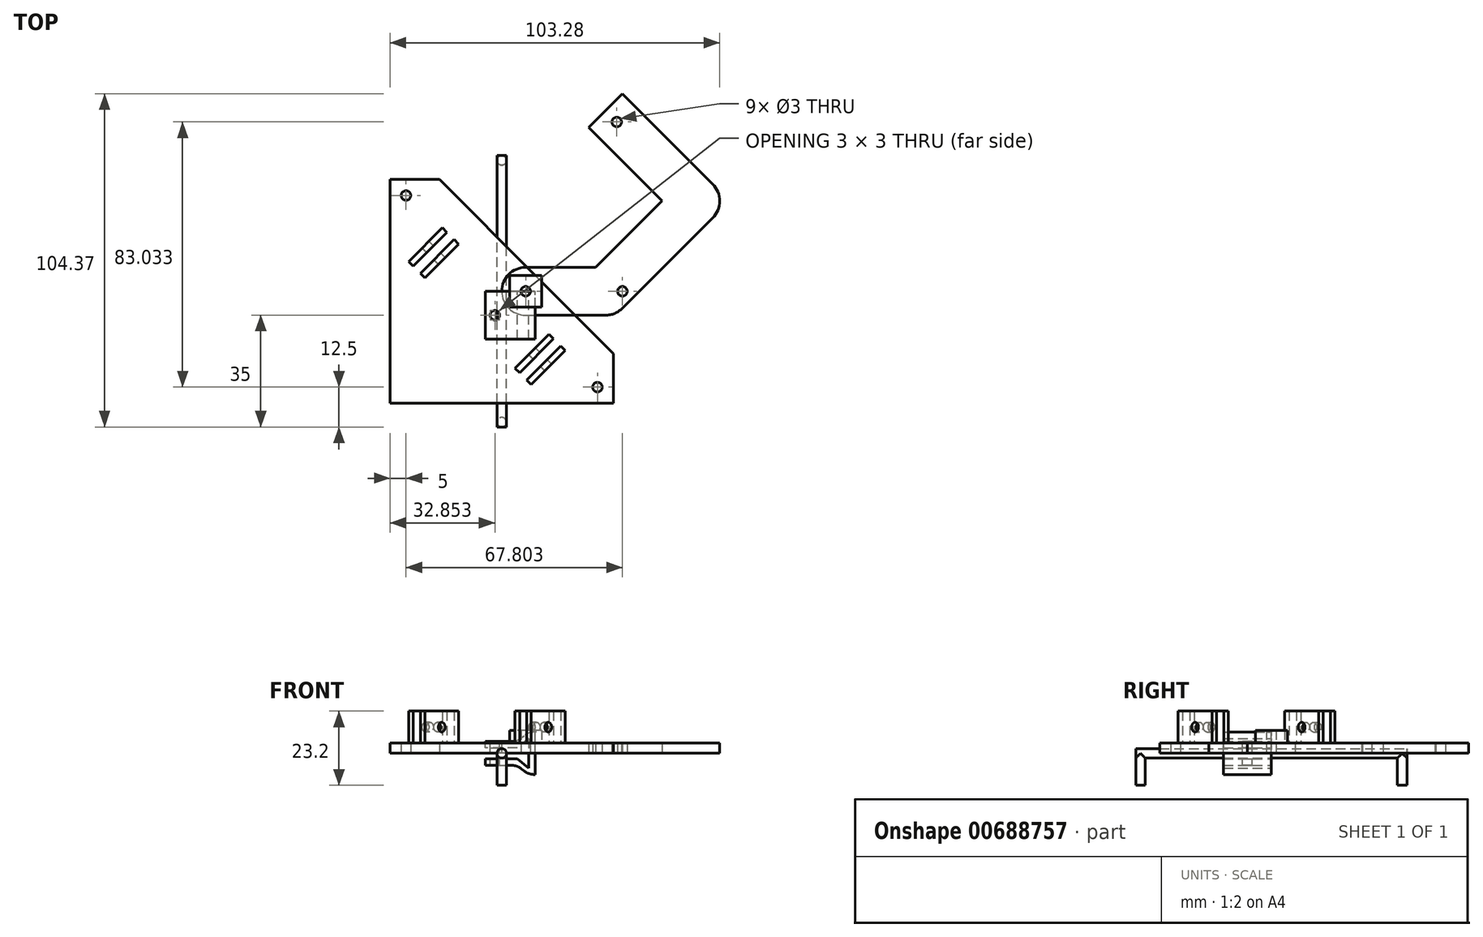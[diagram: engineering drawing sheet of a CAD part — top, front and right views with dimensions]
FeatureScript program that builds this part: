
annotation { "Feature Type Name" : "Feature", "Feature Type Description" : "" }
export const myFeature = defineFeature(function(context is Context, id is Id, definition is map)
    precondition{}
    {
        {
            var Q0;
            Q0=qCreatedBy(makeId("Top.planeOp"),FACE);
            var sketch = newSketch(context, id + "F0", { "sketchPlane" : qUnion([Q0])});
            skArc(sketch, "E0", {"start": v(7.5, 7.5) * mm, "mid": v(0, 0) * mm, "end": v(7.5, -7.5) * mm});
            skPoint(sketch, "E1", {"position": v(0, 0) * mm});
            skArc(sketch, "E2", {"start": v(32.5, -7.5) * mm, "mid": v(39.43, 2.87) * mm, "end": v(27.2, 5.3) * mm});
            skArc(sketch, "E3", {"start": v(55.48, 22.98) * mm, "mid": v(68.28, 28.28) * mm, "end": v(55.48, 33.59) * mm});
            skLineSegment(sketch, "E4", {"start": v(7.5, 7.5) * mm, "end": v(32.5, 7.5) * mm});
            skLineSegment(sketch, "E5", {"start": v(7.5, -7.5) * mm, "end": v(32.5, -7.5) * mm});
            skLineSegment(sketch, "E6", {"start": v(37.8, -5.3) * mm, "end": v(66.09, 22.98) * mm});
            skLineSegment(sketch, "E7", {"start": v(27.2, 5.3) * mm, "end": v(55.48, 33.59) * mm});
            skLineSegment(sketch, "E8", {"start": v(55.48, 22.98) * mm, "end": v(27.2, 51.27) * mm});
            skLineSegment(sketch, "E9", {"start": v(27.2, 51.27) * mm, "end": v(37.8, 61.87) * mm});
            skLineSegment(sketch, "E10", {"start": v(37.8, 61.87) * mm, "end": v(66.09, 33.59) * mm});
            skLineSegment(sketch, "E11", {"start": v(37.8, 61.87) * mm, "end": v(37.8, -5.3) * mm, "construction": true});
            skCircle(sketch, "E12", {"center": v(7.5, 0) * mm, "radius": 1.5 * mm});
            skCircle(sketch, "E13", {"center": v(37.8, 0) * mm, "radius": 1.5 * mm});
            skCircle(sketch, "E14", {"center": v(36.04, 53.03) * mm, "radius": 1.5 * mm});
            skSolve(sketch);
        }
        {
            var Q0;
            Q0=qSketchRegion(id+"F0",true);
            extrude(context, id + "F1", {"entities" : qUnion([Q0]), "depth" : 3.2 * mm, "offsetDistance" : 25 * mm});
        }
        {
            var Q0;
            Q0=qCreatedBy(makeId("Top.planeOp"),FACE);
            var sketch = newSketch(context, id + "F2", { "sketchPlane" : qUnion([Q0])});
            skLineSegment(sketch, "E15.bottom", {"start": v(35, -35) * mm, "end": v(-35, -35) * mm});
            skLineSegment(sketch, "E15.top", {"start": v(-19.55, 35) * mm, "end": v(-35, 35) * mm});
            skLineSegment(sketch, "E15.left", {"start": v(35, -35) * mm, "end": v(35, -19.55) * mm});
            skLineSegment(sketch, "E15.right", {"start": v(-35, -35) * mm, "end": v(-35, 35) * mm});
            skPoint(sketch, "E15.middle", {"position": v(0, 0) * mm});
            skCircle(sketch, "E16", {"center": v(-30, 30) * mm, "radius": 1.5 * mm});
            skCircle(sketch, "E17", {"center": v(30, -30) * mm, "radius": 1.5 * mm});
            skLineSegment(sketch, "E18", {"start": v(-35, 35) * mm, "end": v(35, -35) * mm, "construction": true});
            skLineSegment(sketch, "E19", {"start": v(-19.55, 35) * mm, "end": v(35, -19.55) * mm});
            skSolve(sketch);
        }
        {
            var Q0;
            Q0=makeQuery(id+"F2.imprint","IMPRINT",FACE,{"disambiguationData":[TD([[makeQuery(id+"F2.imprint","IMPRINT",EDGE,{"derivedFrom":sQuery(id+"F2.wireOp",EDGE,"E15.bottom")}),-1.0]])]});
            extrude(context, id + "F3", {"entities" : qUnion([Q0]), "depth" : 3.2 * mm, "offsetDistance" : 25 * mm});
        }
        {
            var Q0;
            Q0=qCreatedBy(makeId("Front.planeOp"),FACE);
            var sketch = newSketch(context, id + "F4", { "sketchPlane" : qUnion([Q0])});
            skLineSegment(sketch, "E20", {"start": v(8.43, -4.62) * mm, "end": v(4.85, -1.75) * mm});
            skLineSegment(sketch, "E21", {"start": v(4.85, -1.75) * mm, "end": v(-5.15, -1.75) * mm});
            skLineSegment(sketch, "E22", {"start": v(-5.15, -1.75) * mm, "end": v(-5.15, -3.75) * mm});
            skLineSegment(sketch, "E23", {"start": v(-5.15, -3.75) * mm, "end": v(4.85, -3.75) * mm});
            skLineSegment(sketch, "E24", {"start": v(4.85, -3.75) * mm, "end": v(8.43, -6.62) * mm});
            skLineSegment(sketch, "E25", {"start": v(8.43, -6.62) * mm, "end": v(10.43, -6.62) * mm});
            skPoint(sketch, "E26", {"position": v(8.43, 0) * mm});
            skPoint(sketch, "E27", {"position": v(10.43, 0) * mm});
            skLineSegment(sketch, "E28", {"start": v(10.43, 0) * mm, "end": v(-7.22, 0) * mm, "construction": true});
            skLineSegment(sketch, "E29", {"start": v(8.43, -4.62) * mm, "end": v(8.43, 0) * mm});
            skLineSegment(sketch, "E30", {"start": v(10.43, -6.62) * mm, "end": v(10.43, 0) * mm});
            skLineSegment(sketch, "E31.MirrorCS", {"start": v(-5.15, 1.75) * mm, "end": v(-5.15, 3.75) * mm});
            skLineSegment(sketch, "E32.MirrorCS", {"start": v(8.43, 6.62) * mm, "end": v(10.43, 6.62) * mm});
            skLineSegment(sketch, "E33.MirrorCS", {"start": v(4.85, 1.75) * mm, "end": v(-5.15, 1.75) * mm});
            skLineSegment(sketch, "E34.MirrorCS", {"start": v(8.43, 4.62) * mm, "end": v(4.85, 1.75) * mm});
            skLineSegment(sketch, "E35.MirrorCS", {"start": v(4.85, 3.75) * mm, "end": v(8.43, 6.62) * mm});
            skLineSegment(sketch, "E36.MirrorCS", {"start": v(-5.15, 3.75) * mm, "end": v(4.85, 3.75) * mm});
            skLineSegment(sketch, "E37.MirrorCS", {"start": v(8.43, 4.62) * mm, "end": v(8.43, 0) * mm});
            skLineSegment(sketch, "E38.MirrorCS", {"start": v(10.43, 6.62) * mm, "end": v(10.43, 0) * mm});
            skSolve(sketch);
        }
        {
            var Q0;
            Q0=qSketchRegion(id+"F4",true);
            extrude(context, id + "F5", {"entities" : qUnion([Q0]), "depth" : 15 * mm, "offsetDistance" : 25 * mm});
        }
        {
            var Q0;
            Q0=makeQuery(id+"F5.opExtrude","SWEPT_FACE",FACE,{"disambiguationData":[OSD([sQuery(id+"F4.wireOp",EDGE,"E36.MirrorCS")])]});
            var sketch = newSketch(context, id + "F6", { "sketchPlane" : qUnion([Q0])});
            skCircle(sketch, "E39", {"center": v(-2.15, -7.5) * mm, "radius": 1.5 * mm});
            skSolve(sketch);
        }
        {
            var Q0;
            Q0=makeQuery(id+"F6.imprint","IMPRINT",FACE,{"disambiguationData":[TD([[makeQuery(id+"F6.imprint","IMPRINT",EDGE,{"derivedFrom":sQuery(id+"F6.wireOp",EDGE,"E39")}),1.0]])]});
            extrude(context, id + "F7", {"entities" : qUnion([Q0]), "operationType" : NewBodyOperationType.REMOVE, "oppositeDirection" : true, "depth" : 25 * mm, "offsetDistance" : 25 * mm});
        }
        {
            var Q0;
            Q0=makeQuery(id+"F5.opExtrude","SWEPT_EDGE",EDGE,{"disambiguationData":[OSD([sQuery(id+"F4.wireOp",EDGE,"E35.MirrorCS"),sQuery(id+"F4.wireOp",EDGE,"E36.MirrorCS")])]});
            fillet(context, id + "F8", {"entities" : qUnion([Q0]), "radius" : 5 * mm, "tangentPropagation" : true, "allowEdgeOverflow" : false});
        }
        {
            var Q0;
            Q0=makeQuery(id+"F5.opExtrude","SWEPT_EDGE",EDGE,{"disambiguationData":[OSD([sQuery(id+"F4.wireOp",EDGE,"E23"),sQuery(id+"F4.wireOp",EDGE,"E24")])]});
            var Q1;
            Q1=makeQuery(id+"F5.opExtrude","SWEPT_EDGE",EDGE,{"disambiguationData":[OSD([sQuery(id+"F4.wireOp",EDGE,"E24"),sQuery(id+"F4.wireOp",EDGE,"E25")])]});
            var Q2;
            Q2=makeQuery(id+"F5.opExtrude","SWEPT_EDGE",EDGE,{"disambiguationData":[OSD([sQuery(id+"F4.wireOp",EDGE,"E32.MirrorCS"),sQuery(id+"F4.wireOp",EDGE,"E35.MirrorCS")])]});
            fillet(context, id + "F9", {"entities" : qUnion([Q0, Q1, Q2]), "radius" : 5 * mm, "tangentPropagation" : true, "allowEdgeOverflow" : false});
        }
        {
            var Q0;
            Q0=makeQuery(id+"F1.opExtrude","CAP_FACE",FACE,{"disambiguationData":[OSD([sQuery(id+"F0.wireOp",EDGE,"E0"),sQuery(id+"F0.wireOp",EDGE,"E2"),sQuery(id+"F0.wireOp",EDGE,"E3"),sQuery(id+"F0.wireOp",EDGE,"E4"),sQuery(id+"F0.wireOp",EDGE,"E5"),sQuery(id+"F0.wireOp",EDGE,"E6"),sQuery(id+"F0.wireOp",EDGE,"E7"),sQuery(id+"F0.wireOp",EDGE,"E8"),sQuery(id+"F0.wireOp",EDGE,"E9"),sQuery(id+"F0.wireOp",EDGE,"E10"),sQuery(id+"F0.wireOp",EDGE,"E12"),sQuery(id+"F0.wireOp",EDGE,"E13"),sQuery(id+"F0.wireOp",EDGE,"E14")])],"isStart":false});
            var sketch = newSketch(context, id + "F10", { "sketchPlane" : qUnion([Q0])});
            skLineSegment(sketch, "E40.bottom", {"start": v(12.5, -5) * mm, "end": v(2.5, -5) * mm});
            skLineSegment(sketch, "E40.top", {"start": v(12.5, 5) * mm, "end": v(2.5, 5) * mm});
            skLineSegment(sketch, "E40.left", {"start": v(12.5, -5) * mm, "end": v(12.5, 5) * mm});
            skLineSegment(sketch, "E40.right", {"start": v(2.5, -5) * mm, "end": v(2.5, 5) * mm});
            skPoint(sketch, "E40.middle", {"position": v(7.5, 0) * mm});
            skSolve(sketch);
        }
        {
            var Q0;
            Q0=makeQuery(id+"F10.imprint","IMPRINT",FACE,{"disambiguationData":[TD([[makeQuery(id+"F10.imprint","IMPRINT",EDGE,{"derivedFrom":sQuery(id+"F10.wireOp",EDGE,"E40.bottom")}),-1.0]])]});
            extrude(context, id + "F11", {"entities" : qUnion([Q0]), "depth" : 4 * mm, "offsetDistance" : 25 * mm});
        }
        {
            var Q0;
            Q0=makeQuery(id+"F3.opExtrude","CAP_FACE",FACE,{"disambiguationData":[OSD([sQuery(id+"F2.wireOp",EDGE,"E15.bottom"),sQuery(id+"F2.wireOp",EDGE,"E15.top"),sQuery(id+"F2.wireOp",EDGE,"E15.left"),sQuery(id+"F2.wireOp",EDGE,"E15.right"),sQuery(id+"F2.wireOp",EDGE,"E16"),sQuery(id+"F2.wireOp",EDGE,"E17"),sQuery(id+"F2.wireOp",EDGE,"E19")])],"isStart":true});
            var sketch = newSketch(context, id + "F12", { "sketchPlane" : qUnion([Q0])});
            skLineSegment(sketch, "E41", {"start": v(-25.5, -5.6) * mm, "end": v(-14.9, -16.2) * mm});
            skLineSegment(sketch, "E42", {"start": v(14.8, 13.49) * mm, "end": v(4.19, 24.1) * mm});
            skLineSegment(sketch, "E43", {"start": v(-25.5, -5.6) * mm, "end": v(-24.1, -4.19) * mm});
            skLineSegment(sketch, "E44", {"start": v(-14.9, -16.2) * mm, "end": v(-13.49, -14.8) * mm});
            skLineSegment(sketch, "E45", {"start": v(-13.49, -14.8) * mm, "end": v(-24.1, -4.19) * mm});
            skLineSegment(sketch, "E46", {"start": v(4.19, 24.1) * mm, "end": v(5.6, 25.5) * mm});
            skLineSegment(sketch, "E47", {"start": v(5.6, 25.5) * mm, "end": v(16.2, 14.9) * mm});
            skLineSegment(sketch, "E48", {"start": v(16.2, 14.9) * mm, "end": v(14.8, 13.49) * mm});
            skLineSegment(sketch, "E49", {"start": v(-8.96, -24.41) * mm, "end": v(-29.1, -4.27) * mm, "construction": true});
            skLineSegment(sketch, "E50.MirrorCS", {"start": v(-27.77, -7.87) * mm, "end": v(-29.19, -9.28) * mm});
            skLineSegment(sketch, "E51.MirrorCS", {"start": v(-18.58, -19.89) * mm, "end": v(-29.19, -9.28) * mm});
            skLineSegment(sketch, "E52.MirrorCS", {"start": v(-27.77, -7.87) * mm, "end": v(-17.17, -18.47) * mm});
            skLineSegment(sketch, "E53.MirrorCS", {"start": v(-17.17, -18.47) * mm, "end": v(-18.58, -19.89) * mm});
            skLineSegment(sketch, "E54", {"start": v(24.41, 8.96) * mm, "end": v(5.32, 28.06) * mm, "construction": true});
            skLineSegment(sketch, "E55.MirrorCS", {"start": v(7.87, 27.77) * mm, "end": v(18.47, 17.17) * mm});
            skLineSegment(sketch, "E56.MirrorCS", {"start": v(19.89, 18.58) * mm, "end": v(9.28, 29.19) * mm});
            skLineSegment(sketch, "E57.MirrorCS", {"start": v(18.47, 17.17) * mm, "end": v(19.89, 18.58) * mm});
            skLineSegment(sketch, "E58.MirrorCS", {"start": v(9.28, 29.19) * mm, "end": v(7.87, 27.77) * mm});
            skSolve(sketch);
        }
        {
            var Q0;
            Q0=makeQuery(id+"F12.imprint","IMPRINT",FACE,{"disambiguationData":[TD([[makeQuery(id+"F12.imprint","IMPRINT",EDGE,{"derivedFrom":sQuery(id+"F12.wireOp",EDGE,"E50.MirrorCS")}),1.0]])]});
            var Q1;
            Q1=makeQuery(id+"F12.imprint","IMPRINT",FACE,{"disambiguationData":[TD([[makeQuery(id+"F12.imprint","IMPRINT",EDGE,{"derivedFrom":sQuery(id+"F12.wireOp",EDGE,"E41")}),1.0]])]});
            var Q2;
            Q2=makeQuery(id+"F12.imprint","IMPRINT",FACE,{"disambiguationData":[TD([[makeQuery(id+"F12.imprint","IMPRINT",EDGE,{"derivedFrom":sQuery(id+"F12.wireOp",EDGE,"E42")}),-1.0]])]});
            var Q3;
            Q3=makeQuery(id+"F12.imprint","IMPRINT",FACE,{"disambiguationData":[TD([[makeQuery(id+"F12.imprint","IMPRINT",EDGE,{"derivedFrom":sQuery(id+"F12.wireOp",EDGE,"E55.MirrorCS")}),1.0]])]});
            extrude(context, id + "F13", {"entities" : qUnion([Q0, Q1, Q2, Q3]), "operationType" : NewBodyOperationType.ADD, "oppositeDirection" : true, "depth" : 13.2 * mm, "offsetDistance" : 25 * mm});
        }
        {
            var Q0;
            Q0=makeQuery(id+"F13.opExtrude","SWEPT_FACE",FACE,{"disambiguationData":[OSD([sQuery(id+"F12.wireOp",EDGE,"E51.MirrorCS")])]});
            var sketch = newSketch(context, id + "F14", { "sketchPlane" : qUnion([Q0])});
            skCircle(sketch, "E59", {"center": v(6.58, 8.2) * mm, "radius": 1.5 * mm});
            skPoint(sketch, "E59.centerSnap0", {"position": v(6.58, 13.2) * mm});
            skSolve(sketch);
        }
        {
            var Q0;
            Q0=makeQuery(id+"F14.imprint","IMPRINT",FACE,{"disambiguationData":[TD([[makeQuery(id+"F14.imprint","IMPRINT",EDGE,{"derivedFrom":sQuery(id+"F14.wireOp",EDGE,"E59")}),1.0]])]});
            var Q1;
            Q1=sQuery(id+"F14.wireOp",EDGE,"E59");
            extrude(context, id + "F15", {"entities" : qUnion([Q0]), "operationType" : NewBodyOperationType.REMOVE, "surfaceEntities" : qUnion([Q1]), "oppositeDirection" : true, "depth" : 60 * mm, "offsetDistance" : 25 * mm});
        }
        {
            var Q0;
            Q0=qCreatedBy(makeId("Front.planeOp"),FACE);
            var sketch = newSketch(context, id + "F16", { "sketchPlane" : qUnion([Q0])});
            skCircle(sketch, "E60", {"center": v(0, 0) * mm, "radius": 1.5 * mm});
            skSolve(sketch);
        }
        {
            var Q0;
            Q0=makeQuery(id+"F16.imprint","IMPRINT",FACE,{"disambiguationData":[TD([[makeQuery(id+"F16.imprint","IMPRINT",EDGE,{"derivedFrom":sQuery(id+"F16.wireOp",EDGE,"E60")}),1.0]])]});
            var Q1;
            Q1=sQuery(id+"F16.wireOp",EDGE,"E60");
            extrude(context, id + "F17", {"entities" : qUnion([Q0]), "surfaceEntities" : qUnion([Q1]), "depth" : 85 * mm, "offsetDistance" : 25 * mm, "symmetric" : true});
        }
        {
            var Q0;
            Q0=qCreatedBy(makeId("Top.planeOp"),FACE);
            var sketch = newSketch(context, id + "F18", { "sketchPlane" : qUnion([Q0])});
            skCircle(sketch, "E61", {"center": v(0, -41) * mm, "radius": 1.5 * mm});
            skSolve(sketch);
        }
        {
            var Q0;
            Q0=qSketchRegion(id+"F18",true);
            var Q1;
            Q1=sQuery(id+"F18.wireOp",EDGE,"E61");
            extrude(context, id + "F19", {"entities" : qUnion([Q0]), "operationType" : NewBodyOperationType.ADD, "surfaceEntities" : qUnion([Q1]), "oppositeDirection" : true, "depth" : 10 * mm, "offsetDistance" : 25 * mm});
        }
        {
            var Q0;
            Q0=qCreatedBy(makeId("Top.planeOp"),FACE);
            var sketch = newSketch(context, id + "F20", { "sketchPlane" : qUnion([Q0])});
            skCircle(sketch, "E62", {"center": v(0, 41) * mm, "radius": 1.5 * mm});
            skSolve(sketch);
        }
        {
            var Q0;
            Q0=qSketchRegion(id+"F20",true);
            extrude(context, id + "F21", {"entities" : qUnion([Q0]), "operationType" : NewBodyOperationType.ADD, "oppositeDirection" : true, "depth" : 10 * mm, "offsetDistance" : 25 * mm});
        }
    });
